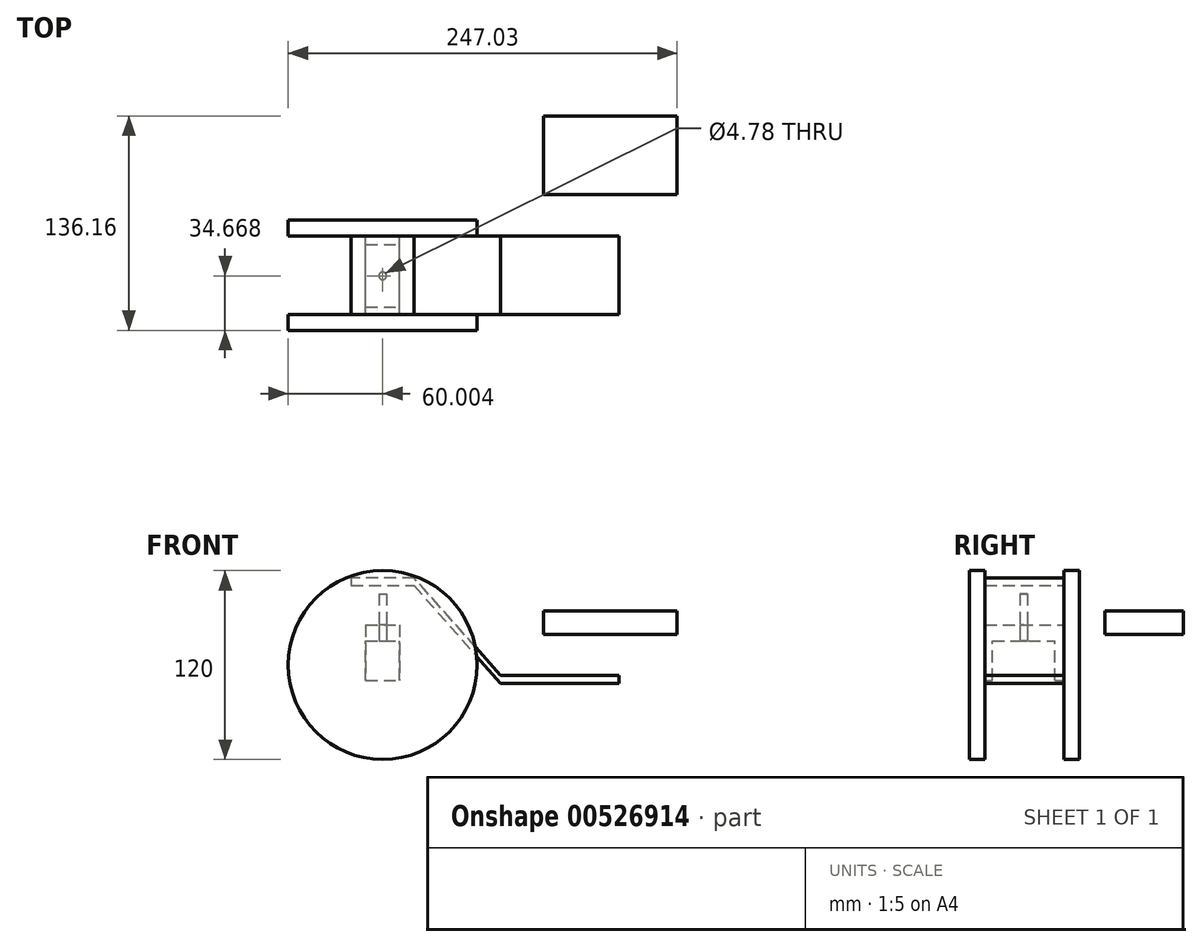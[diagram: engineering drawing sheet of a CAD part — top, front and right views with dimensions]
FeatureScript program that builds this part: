
annotation { "Feature Type Name" : "Feature", "Feature Type Description" : "" }
export const myFeature = defineFeature(function(context is Context, id is Id, definition is map)
    precondition{}
    {
        {
            var Q0;
            Q0=qCreatedBy(makeId("Front.planeOp"),FACE);
            var sketch = newSketch(context, id + "F0", { "sketchPlane" : qUnion([Q0])});
            skLineSegment(sketch, "E0", {"start": v(-108.18, 36.1) * mm, "end": v(-108.18, 31.1) * mm});
            skLineSegment(sketch, "E1", {"start": v(-108.18, 31.1) * mm, "end": v(-68.18, 31.1) * mm});
            skLineSegment(sketch, "E2", {"start": v(-68.18, 31.1) * mm, "end": v(-13.18, -31) * mm});
            skLineSegment(sketch, "E3", {"start": v(-13.18, -31) * mm, "end": v(61.82, -31) * mm});
            skLineSegment(sketch, "E4", {"start": v(61.82, -31) * mm, "end": v(61.82, -26) * mm});
            skLineSegment(sketch, "E5", {"start": v(61.82, -26) * mm, "end": v(-13.18, -26) * mm});
            skLineSegment(sketch, "E6", {"start": v(-13.18, -26) * mm, "end": v(-68.18, 36.1) * mm});
            skLineSegment(sketch, "E7", {"start": v(-68.18, 36.1) * mm, "end": v(-108.18, 36.1) * mm});
            skLineSegment(sketch, "E8.bottom", {"start": v(-98.9, 6.2) * mm, "end": v(-77.44, 6.2) * mm});
            skLineSegment(sketch, "E8.top", {"start": v(-98.9, -4.04) * mm, "end": v(-77.44, -4.04) * mm});
            skLineSegment(sketch, "E8.left", {"start": v(-98.9, 6.2) * mm, "end": v(-98.9, -4.04) * mm});
            skLineSegment(sketch, "E8.right", {"start": v(-77.44, 6.2) * mm, "end": v(-77.44, -4.04) * mm});
            skLineSegment(sketch, "E9", {"start": v(-88.18, 6.2) * mm, "end": v(-88.18, 31.1) * mm, "construction": true});
            skSolve(sketch);
        }
        {
            var Q0;
            Q0 = qSketchRegion(id + "F0", true);
            extrude(context, id + "F1", {"entities" : qUnion([Q0]), "depth" : 50 * mm, "offsetDistance" : 25 * mm});
        }
        {
            var Q0;
            Q0=makeQuery(id+"F1.opExtrude","SWEPT_FACE",FACE,{"disambiguationData":[OSD([sQuery(id+"F0.wireOp",EDGE,"E8.top")])]});
            var sketch = newSketch(context, id + "F2", { "sketchPlane" : qUnion([Q0])});
            skLineSegment(sketch, "E10.bottom", {"start": v(-98.9, 50) * mm, "end": v(-77.44, 50) * mm});
            skLineSegment(sketch, "E10.top", {"start": v(-98.9, 45.25) * mm, "end": v(-77.44, 45.25) * mm});
            skLineSegment(sketch, "E10.left", {"start": v(-98.9, 50) * mm, "end": v(-98.9, 45.25) * mm});
            skLineSegment(sketch, "E10.right", {"start": v(-77.44, 50) * mm, "end": v(-77.44, 45.25) * mm});
            skLineSegment(sketch, "E11.bottom", {"start": v(-98.9, 0) * mm, "end": v(-77.44, 0) * mm});
            skLineSegment(sketch, "E11.top", {"start": v(-98.9, 5.42) * mm, "end": v(-77.44, 5.42) * mm});
            skLineSegment(sketch, "E11.left", {"start": v(-98.9, 0) * mm, "end": v(-98.9, 5.42) * mm});
            skLineSegment(sketch, "E11.right", {"start": v(-77.44, 0) * mm, "end": v(-77.44, 5.42) * mm});
            skSolve(sketch);
        }
        {
            var Q0;
            Q0=makeQuery(id+"F2.imprint","IMPRINT",FACE,{"disambiguationData":[TD([[makeQuery(id+"F2.imprint","IMPRINT",EDGE,{"derivedFrom":sQuery(id+"F2.wireOp",EDGE,"E10.bottom")}),-1.0]])]});
            var Q1;
            Q1=makeQuery(id+"F2.imprint","IMPRINT",FACE,{"disambiguationData":[TD([[makeQuery(id+"F2.imprint","IMPRINT",EDGE,{"derivedFrom":sQuery(id+"F2.wireOp",EDGE,"E11.bottom")}),1.0]])]});
            extrude(context, id + "F3", {"entities" : qUnion([Q0, Q1]), "operationType" : NewBodyOperationType.ADD, "depth" : 25 * mm, "offsetDistance" : 25 * mm});
        }
        {
            var Q0;
            Q0=makeQuery(id+"F3.boolean.opBoolean","MERGE",FACE,{"derivedFrom":[makeQuery(id+"F1.opExtrude","CAP_FACE",FACE,{"disambiguationData":[OSD([sQuery(id+"F0.wireOp",EDGE,"E8.bottom"),sQuery(id+"F0.wireOp",EDGE,"E8.top"),sQuery(id+"F0.wireOp",EDGE,"E8.left"),sQuery(id+"F0.wireOp",EDGE,"E8.right")])],"isStart":false}),makeQuery(id+"F3.opExtrude","SWEPT_FACE",FACE,{"disambiguationData":[OSD([sQuery(id+"F2.wireOp",EDGE,"E10.bottom")])]})]});
            var sketch = newSketch(context, id + "F4", { "sketchPlane" : qUnion([Q0])});
            skCircle(sketch, "E12", {"center": v(-88.18, -19.26) * mm, "radius": 60 * mm});
            skPoint(sketch, "E12.centerSnap0", {"position": v(-88.18, -29.04) * mm});
            skSolve(sketch);
        }
        {
            var Q0;
            {var subQ1=sQuery(id+"F2.wireOp",EDGE,"E10.bottom");var subQ6=makeQuery(id+"F3.opExtrude","CAP_EDGE",EDGE,{"disambiguationData":[OSD([subQ1])],"isStart":false});Q0=makeQuery(id+"F4.imprint","IMPRINT",FACE,{"disambiguationData":[TD([[makeQuery(id+"F4.imprint","IMPRINT",EDGE,{"derivedFrom":subQ6}),-1.0]])]});}
            var Q1;
            {var subQ1=sQuery(id+"F2.wireOp",EDGE,"E10.bottom");var subQ6=makeQuery(id+"F3.opExtrude","CAP_EDGE",EDGE,{"disambiguationData":[OSD([subQ1])],"isStart":false});Q1=makeQuery(id+"F4.imprint","IMPRINT",FACE,{"disambiguationData":[TD([[makeQuery(id+"F4.imprint","IMPRINT",EDGE,{"derivedFrom":subQ6}),1.0]])]});}
            extrude(context, id + "F5", {"entities" : qUnion([Q0, Q1]), "depth" : 10 * mm, "offsetDistance" : 25 * mm});
        }
        {
            var Q0;
            Q0 = qSketchRegion(id + "F4", true);
            var Q1;
            Q1=makeQuery(id+"F3.boolean.opBoolean","MERGE",FACE,{"derivedFrom":[makeQuery(id+"F1.opExtrude","CAP_FACE",FACE,{"disambiguationData":[OSD([sQuery(id+"F0.wireOp",EDGE,"E8.bottom"),sQuery(id+"F0.wireOp",EDGE,"E8.top"),sQuery(id+"F0.wireOp",EDGE,"E8.left"),sQuery(id+"F0.wireOp",EDGE,"E8.right")])],"isStart":true}),makeQuery(id+"F3.opExtrude","SWEPT_FACE",FACE,{"disambiguationData":[OSD([sQuery(id+"F2.wireOp",EDGE,"E11.bottom")])]})]});
            extrude(context, id + "F6", {"entities" : qUnion([Q0]), "oppositeDirection" : true, "depth" : 60 * mm, "offsetDistance" : 25 * mm, "hasSecondDirection" : true, "secondDirectionBound" : SecondDirectionBoundingType.UP_TO_SURFACE, "secondDirectionOppositeDirection" : true, "secondDirectionDepth" : 25 * mm, "secondDirectionBoundEntityFace" : qUnion([Q1])});
        }
        {
            var Q0;
            Q0=makeQuery(id+"F1.opExtrude","SWEPT_FACE",FACE,{"disambiguationData":[OSD([sQuery(id+"F0.wireOp",EDGE,"E8.top")])]});
            var sketch = newSketch(context, id + "F7", { "sketchPlane" : qUnion([Q0])});
            skCircle(sketch, "E13", {"center": v(-88.18, 25.33) * mm, "radius": 2.4 * mm});
            skPoint(sketch, "E13.centerSnap0", {"position": v(-77.44, 25.33) * mm});
            skPoint(sketch, "E13.centerSnap1", {"position": v(-88.18, 5.42) * mm});
            skSolve(sketch);
        }
        {
            var Q0;
            Q0=makeQuery(id+"F7.imprint","IMPRINT",FACE,{"disambiguationData":[TD([[makeQuery(id+"F7.imprint","IMPRINT",EDGE,{"derivedFrom":sQuery(id+"F7.wireOp",EDGE,"E13")}),1.0]])]});
            extrude(context, id + "F8", {"entities" : qUnion([Q0]), "oppositeDirection" : true, "depth" : 30 * mm, "offsetDistance" : 25 * mm});
        }
        {
            var Q0;
            Q0=makeQuery(id+"F8.opExtrude","SWEPT_BODY",BODY,{"disambiguationData":[OSD([sQuery(id+"F7.wireOp",EDGE,"E13")])]});
            var Q1;
            Q1=makeQuery(id+"F1.opExtrude","SWEPT_BODY",BODY,{"disambiguationData":[OSD([sQuery(id+"F0.wireOp",EDGE,"E0"),sQuery(id+"F0.wireOp",EDGE,"E1"),sQuery(id+"F0.wireOp",EDGE,"E2"),sQuery(id+"F0.wireOp",EDGE,"E3"),sQuery(id+"F0.wireOp",EDGE,"E4"),sQuery(id+"F0.wireOp",EDGE,"E5"),sQuery(id+"F0.wireOp",EDGE,"E6"),sQuery(id+"F0.wireOp",EDGE,"E7")])]});
            var Q2;
            Q2=makeQuery(id+"F1.opExtrude","SWEPT_BODY",BODY,{"disambiguationData":[OSD([sQuery(id+"F0.wireOp",EDGE,"E8.bottom"),sQuery(id+"F0.wireOp",EDGE,"E8.top"),sQuery(id+"F0.wireOp",EDGE,"E8.left"),sQuery(id+"F0.wireOp",EDGE,"E8.right")])]});
            booleanBodies(context, id + "F9", {"operationType" : BooleanOperationType.SUBTRACTION, "tools" : qUnion([Q0]), "targets" : qUnion([Q1, Q2]), "keepTools" : true});
        }
        {
            var Q0;
            Q0=qCreatedBy(makeId("Top.planeOp"),FACE);
            var sketch = newSketch(context, id + "F10", { "sketchPlane" : qUnion([Q0])});
            skLineSegment(sketch, "E14.bottom", {"start": v(13.85, 76.16) * mm, "end": v(98.85, 76.16) * mm});
            skLineSegment(sketch, "E14.top", {"start": v(13.85, 26.16) * mm, "end": v(98.85, 26.16) * mm});
            skLineSegment(sketch, "E14.left", {"start": v(13.85, 76.16) * mm, "end": v(13.85, 26.16) * mm});
            skLineSegment(sketch, "E14.right", {"start": v(98.85, 76.16) * mm, "end": v(98.85, 26.16) * mm});
            skSolve(sketch);
        }
        {
            var Q0;
            Q0=makeQuery(id+"F10.imprint","IMPRINT",FACE,{"disambiguationData":[TD([[makeQuery(id+"F10.imprint","IMPRINT",EDGE,{"derivedFrom":sQuery(id+"F10.wireOp",EDGE,"E14.bottom")}),-1.0]])]});
            extrude(context, id + "F11", {"entities" : qUnion([Q0]), "depth" : 15 * mm, "offsetDistance" : 25 * mm});
        }
    });
